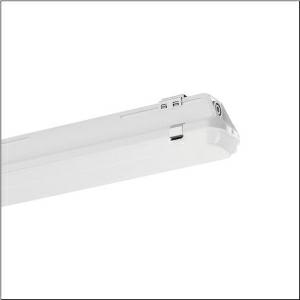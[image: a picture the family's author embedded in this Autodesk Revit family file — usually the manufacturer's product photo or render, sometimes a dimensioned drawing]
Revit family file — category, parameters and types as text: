
# Revit family: monsun_r__11_51fp109p460h_b614
name_source: partatom
category: Lighting Fixtures
units: mm (PartAtom-declared; Revit-internal decimal feet)

## family parameters
Cut with Voids When Loaded = No
Host = Face
Light Source = No
Part Type = Normal
Room Calculation Point = No
Round Connector Dimension = Use Diameter
Shared = No

## types (1)
- Monsun® 11 (1 x LED, 6100 lm, 34 W, 4000K)
    Apparent Load = 34 VA
    CIE Flux Codes = 47 77 93 94 100
    Color Rendering = 80
    Color Temperature = 4000K
    Default Elevation = 1800 mm
    Description = Monsun® 11, damp-proof luminaire, chain hanger, primary optical cover: enclosure, of PMMA, light emission: direct distribution, primary light characteristic: symmetric, installation type: suspended mounting, surface-mounted, horizontal mounting, vertical mounting, LED, rated luminous flux: 6.100lm, luminous efficacy: 179lm/W, light colour: 840, colour temperature: 4000K, control gear: ON/OFF, CLOi, with terminal, 3-pole, max. 2.5mm², mains connection: 220..240V, AC, 50/60Hz, start of lifetime: 34W, end of service life: 38W, luminaire housing, of glass-fibre reinforced polyester, uncoated, bright grey, incl. chain hanger, length: 1.590mm, width: 90mm, height: 88mm, clip for enclosure, of stainless steel (V2A), ceiling mounting element, of stainless steel (V2A), chain hanger, of stainless steel (V2A), protection rating (complete): IP66, insulation class (complete): insulation class I (protective earthing), certification: CE, ENEC, VDE, UKCA, protection symbol: D, impact resistance: IK04, permissible operating ambient temperature: -35..+40°C, standard: EN 50419, EN 60598-2-1, no direct snow, no direct sun, no direct rain, for indoor or canopied outdoor use, corresponds to IFS (International Featured Standards) requirements for safety and quality in the food industry, contact your sales advisor before using the luminaires in applications with unclear chemical exposure, large temperature fluctuations or condensation-forming humidity, LABS conformity tested according to VDMA 24364:2018-05, packaging unit: 1 piece
    Height = 89 mm
    Lamp = 1 x LED
    Lamp Light Flux = 6100 lm
    Lamp Power = 34 W
    Lamp count = 1
    Length = 1590 mm
    Luminous efficacy = 179 lm/W
    Manufacturer = Siteco
    ModVariant = No
    Model = 51FP109P460H
    Mounting Place = Ceiling
    Mounting Type = Surface mounted
    Number of Poles = 1
    OnlyDefault = Yes
    Power Factor = 1
    Product Name = Monsun® 11
    Product group = damp-proof luminaire
    ProductGroupID = 301
    Protection Class = Protection class I
    Protection Degree = IP 66
    RLX_Detail_Level = 1
    RLX_Emergency_Light_Flux = 0 lm
    RLX_Emergency_Type = 0
    RLX_Emergency_Type_DB = No
    RlxData = <blob elided: 88793 chars, md5=52b8c88c>
    Socket = socket
    Standby Power = 0 W
    System Light Flux = 6100 lm
    System Power = 34 W
    Type Comments = Product without accessories
    Type Image = l_1349237.jpg
    URL = http://relux.com
    VarID = ---
    Voltage = 0 V
    Weight = 0.00 kg
    Width = 90 mm

## geometry (parser evidence)
native form markers: Blend x4, Sweep x13
no freeform markers — native parametric forms only
